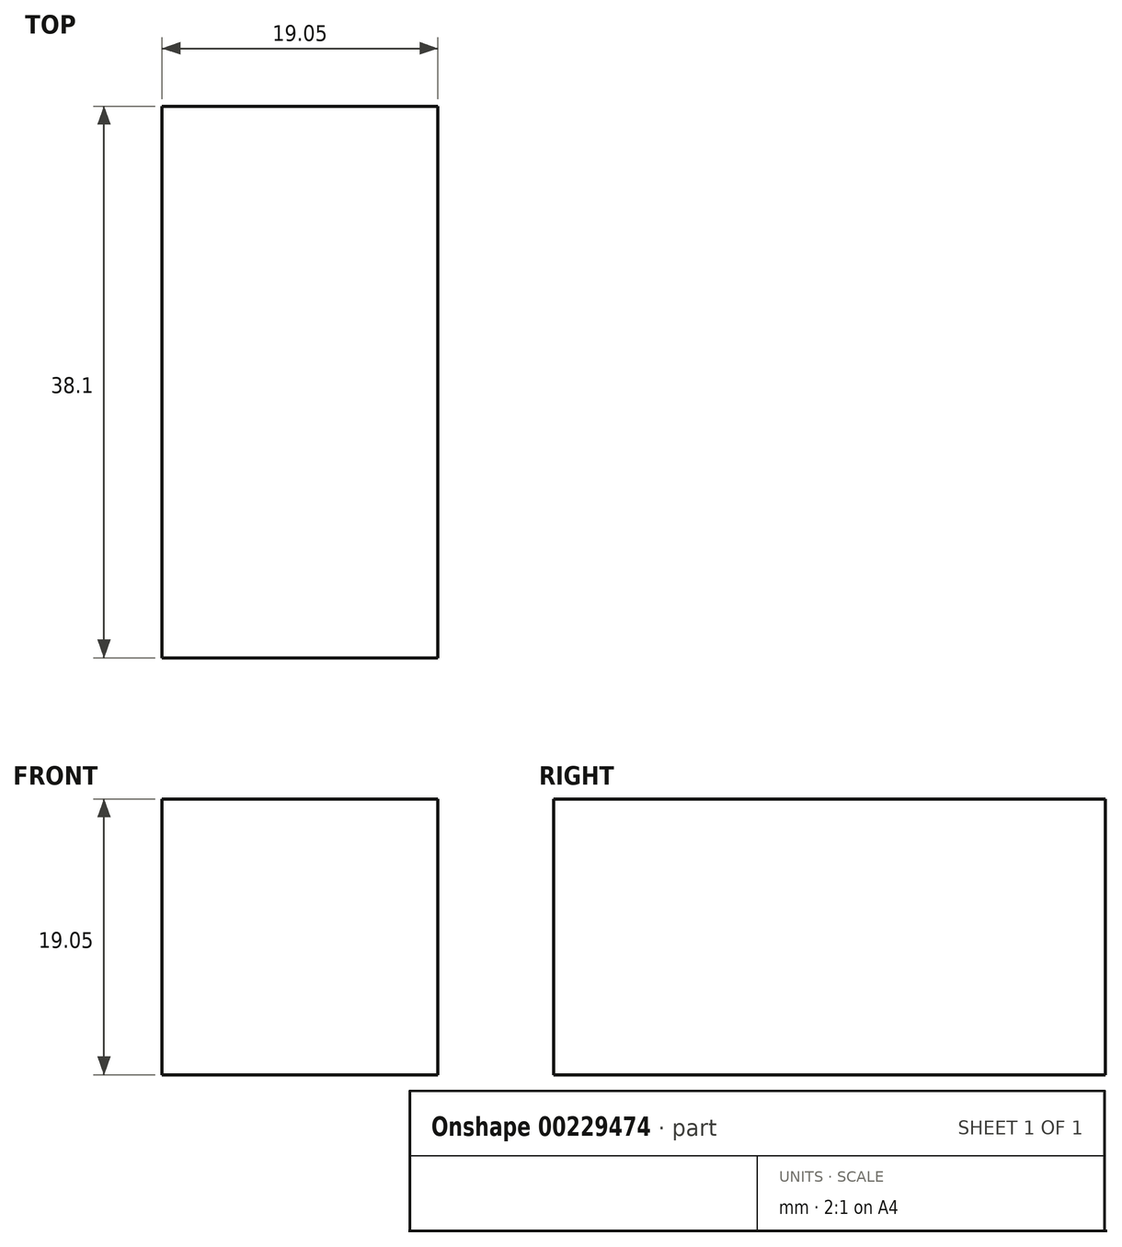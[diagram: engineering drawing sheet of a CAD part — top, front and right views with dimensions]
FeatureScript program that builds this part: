
annotation { "Feature Type Name" : "Feature", "Feature Type Description" : "" }
export const myFeature = defineFeature(function(context is Context, id is Id, definition is map)
    precondition{}
    {
        {
            var Q0;
            Q0=qCreatedBy(makeId("Top.planeOp"),FACE);
            var sketch = newSketch(context, id + "F0", { "sketchPlane" : qUnion([Q0])});
            skLineSegment(sketch, "E0.bottom", {"start": v(-55.26, 0) * mm, "end": v(-36.2, 0) * mm});
            skLineSegment(sketch, "E0.top", {"start": v(-55.26, -38.1) * mm, "end": v(-36.2, -38.1) * mm});
            skLineSegment(sketch, "E0.left", {"start": v(-55.26, 0) * mm, "end": v(-55.26, -38.1) * mm});
            skLineSegment(sketch, "E0.right", {"start": v(-36.2, 0) * mm, "end": v(-36.2, -38.1) * mm});
            skSolve(sketch);
        }
        {
            var Q0;
            Q0 = qSketchRegion(id + "F0", true);
            extrude(context, id + "F1", {"entities" : qUnion([Q0]), "depth" : 19.05 * mm});
        }
    });
